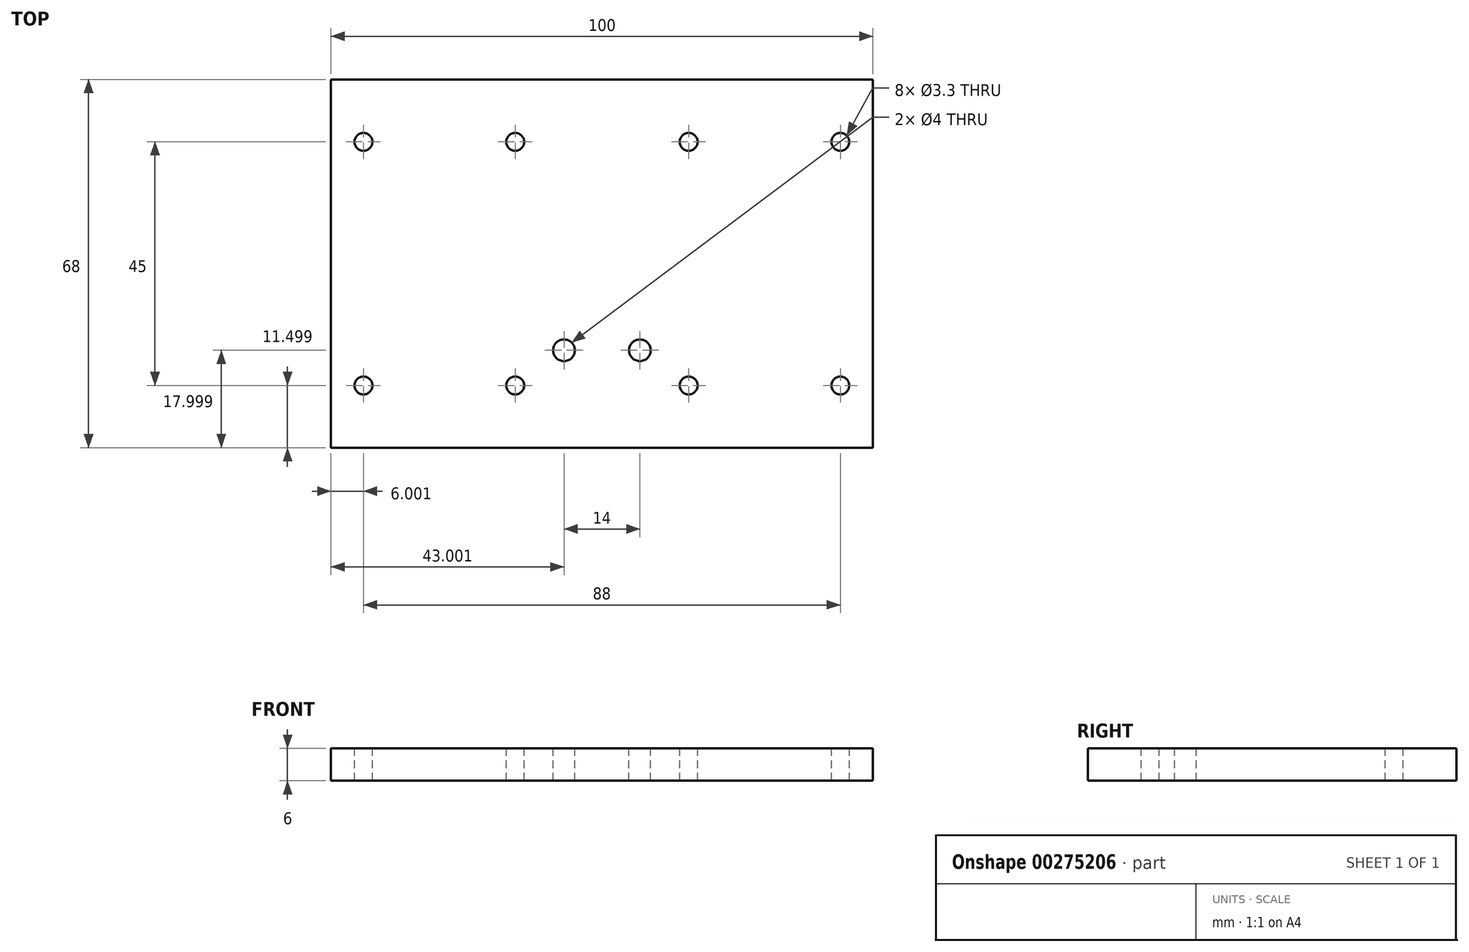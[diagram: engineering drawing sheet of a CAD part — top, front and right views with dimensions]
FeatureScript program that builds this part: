
annotation { "Feature Type Name" : "Feature", "Feature Type Description" : "" }
export const myFeature = defineFeature(function(context is Context, id is Id, definition is map)
    precondition{}
    {
        {
            var Q0;
            Q0=qCreatedBy(makeId("Top.planeOp"),FACE);
            var sketch = newSketch(context, id + "F0", { "sketchPlane" : qUnion([Q0])});
            skLineSegment(sketch, "E0.bottom", {"start": v(-57.06, 32.3) * mm, "end": v(42.94, 32.3) * mm});
            skLineSegment(sketch, "E0.top", {"start": v(-57.06, -35.7) * mm, "end": v(42.94, -35.7) * mm});
            skLineSegment(sketch, "E0.left", {"start": v(-57.06, 32.3) * mm, "end": v(-57.06, -35.7) * mm});
            skLineSegment(sketch, "E0.right", {"start": v(42.94, 32.3) * mm, "end": v(42.94, -35.7) * mm});
            skLineSegment(sketch, "E1", {"start": v(-7.06, 32.3) * mm, "end": v(-7.06, -35.7) * mm, "construction": true});
            skLineSegment(sketch, "E2", {"start": v(-37.06, 32.3) * mm, "end": v(-37.06, -35.7) * mm, "construction": true});
            skLineSegment(sketch, "E3", {"start": v(22.94, 32.3) * mm, "end": v(22.94, -35.7) * mm, "construction": true});
            skLineSegment(sketch, "E4", {"start": v(-51.06, 32.3) * mm, "end": v(-51.06, -35.7) * mm, "construction": true});
            skLineSegment(sketch, "E5", {"start": v(-23.06, 32.3) * mm, "end": v(-23.06, -35.7) * mm, "construction": true});
            skLineSegment(sketch, "E6", {"start": v(8.94, 32.3) * mm, "end": v(8.94, -35.7) * mm, "construction": true});
            skLineSegment(sketch, "E7", {"start": v(36.94, 32.3) * mm, "end": v(36.94, -35.7) * mm, "construction": true});
            skLineSegment(sketch, "E8", {"start": v(-57.06, -1.7) * mm, "end": v(42.94, -1.7) * mm, "construction": true});
            skLineSegment(sketch, "E9", {"start": v(-57.06, -24.2) * mm, "end": v(42.94, -24.2) * mm, "construction": true});
            skLineSegment(sketch, "E10", {"start": v(-57.06, 20.8) * mm, "end": v(42.94, 20.8) * mm, "construction": true});
            skPoint(sketch, "E11", {"position": v(-51.06, 20.8) * mm});
            skPoint(sketch, "E12", {"position": v(-23.06, 20.8) * mm});
            skPoint(sketch, "E13", {"position": v(-51.06, -24.2) * mm});
            skPoint(sketch, "E14", {"position": v(-23.06, -24.2) * mm});
            skPoint(sketch, "E15", {"position": v(8.94, 20.8) * mm});
            skPoint(sketch, "E16", {"position": v(36.94, 20.8) * mm});
            skPoint(sketch, "E17", {"position": v(8.94, -24.2) * mm});
            skPoint(sketch, "E18", {"position": v(36.94, -24.2) * mm});
            skPoint(sketch, "E19", {"position": v(-0.06, -17.7) * mm});
            skPoint(sketch, "E20", {"position": v(-14.06, -17.7) * mm});
            skLineSegment(sketch, "E21", {"start": v(42.94, -17.7) * mm, "end": v(-57.06, -17.7) * mm, "construction": true});
            skSolve(sketch);
        }
        {
            var Q0;
            Q0=makeQuery(id+"F0.imprint","IMPRINT",FACE,{"disambiguationData":[TD([[makeQuery(id+"F0.imprint","IMPRINT",EDGE,{"derivedFrom":sQuery(id+"F0.wireOp",EDGE,"E0.bottom")}),-1.0]])]});
            extrude(context, id + "F1", {"entities" : qUnion([Q0]), "oppositeDirection" : true, "depth" : 6 * mm});
        }
        {
            var Q0;
            Q0=sQuery(id+"F0.wireOp",VERTEX,"E11");
            var Q1;
            Q1=sQuery(id+"F0.wireOp",VERTEX,"E12");
            var Q2;
            Q2=sQuery(id+"F0.wireOp",VERTEX,"E13");
            var Q3;
            Q3=sQuery(id+"F0.wireOp",VERTEX,"E14");
            var Q4;
            Q4=sQuery(id+"F0.wireOp",VERTEX,"E15");
            var Q5;
            Q5=sQuery(id+"F0.wireOp",VERTEX,"E16");
            var Q6;
            Q6=sQuery(id+"F0.wireOp",VERTEX,"E17");
            var Q7;
            Q7=sQuery(id+"F0.wireOp",VERTEX,"E18");
            var Q8;
            Q8=makeQuery(id+"F1.opExtrude","SWEPT_BODY",BODY,{"disambiguationData":[OSD([sQuery(id+"F0.wireOp",EDGE,"E0.bottom"),sQuery(id+"F0.wireOp",EDGE,"E0.top"),sQuery(id+"F0.wireOp",EDGE,"E0.left"),sQuery(id+"F0.wireOp",EDGE,"E0.right")])]});
            hole(context, id + "F2", {"style" : HoleStyle.SIMPLE, "endStyle" : HoleEndStyle.THROUGH, "standardTappedOrClearance" : lookupTablePath({ "standard" : "ISO", "engagement" : "75%", "pitch" : "0.7 mm", "size" : "M4", "type" : "Tapped" }), "standardBlindInLast" : lookupTablePath({ "standard" : "ISO", "engagement" : "75%", "pitch" : "0.7 mm", "size" : "M4", "type" : "Tapped" }), "holeDiameter" : 3.3 * mm, "showTappedDepth" : true, "tappedDepth" : 12 * mm, "tapClearance" : 3, "locations" : qUnion([Q0, Q1, Q2, Q3, Q4, Q5, Q6, Q7]), "scope" : qUnion([Q8]), "isTappedThrough" : true, "majorDiameter" : 4 * mm});
        }
        {
            var Q0;
            Q0=sQuery(id+"F0.wireOp",VERTEX,"E20");
            var Q1;
            Q1=sQuery(id+"F0.wireOp",VERTEX,"E19");
            var Q2;
            Q2=makeQuery(id+"F1.opExtrude","SWEPT_BODY",BODY,{"disambiguationData":[OSD([sQuery(id+"F0.wireOp",EDGE,"E0.bottom"),sQuery(id+"F0.wireOp",EDGE,"E0.top"),sQuery(id+"F0.wireOp",EDGE,"E0.left"),sQuery(id+"F0.wireOp",EDGE,"E0.right")])]});
            hole(context, id + "F3", {"style" : HoleStyle.SIMPLE, "endStyle" : HoleEndStyle.THROUGH, "holeDiameter" : 4 * mm, "isTappedThrough" : true, "tappedDepth" : 12 * mm, "tapClearance" : 3, "startFromSketch" : true, "locations" : qUnion([Q0, Q1]), "scope" : qUnion([Q2])});
        }
    });
